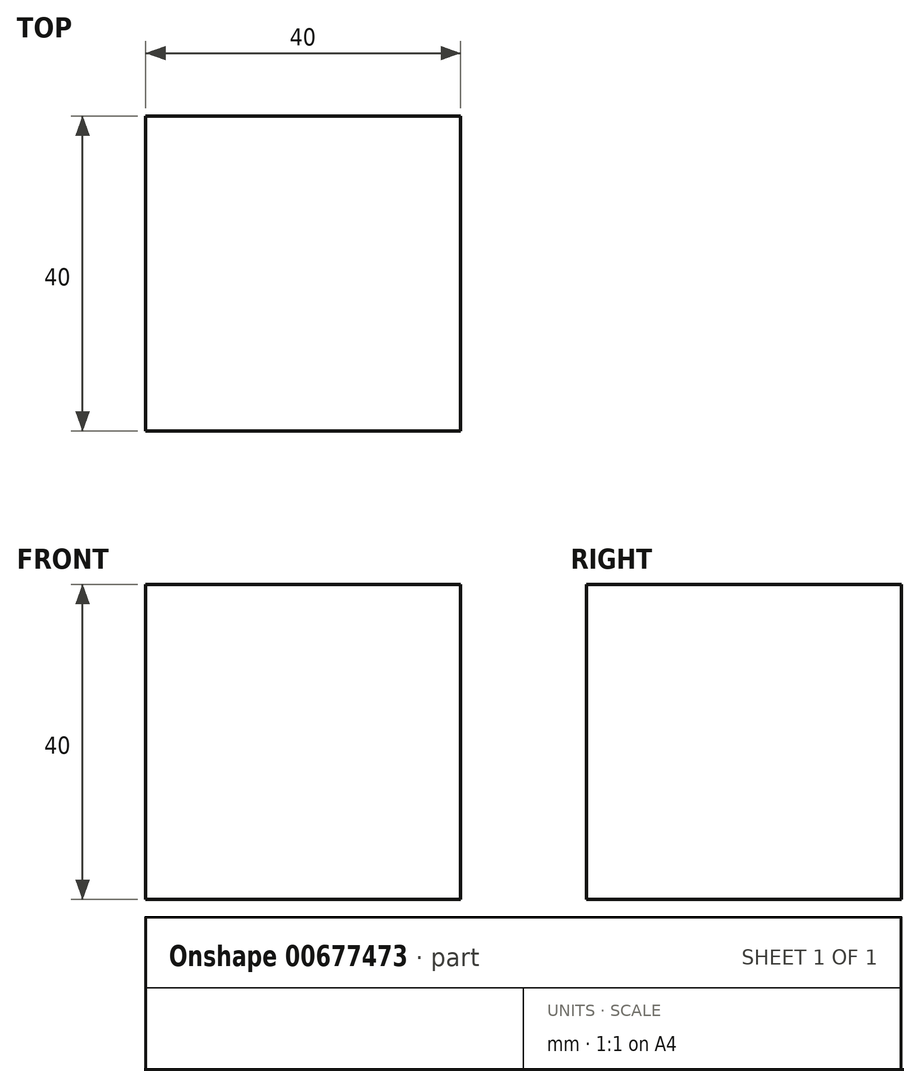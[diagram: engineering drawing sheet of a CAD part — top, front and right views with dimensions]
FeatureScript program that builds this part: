
annotation { "Feature Type Name" : "Feature", "Feature Type Description" : "" }
export const myFeature = defineFeature(function(context is Context, id is Id, definition is map)
    precondition{}
    {
        {
            var Q0;
            Q0=qCreatedBy(makeId("Front.planeOp"),FACE);
            var sketch = newSketch(context, id + "F0", { "sketchPlane" : qUnion([Q0])});
            skLineSegment(sketch, "E0.bottom", {"start": v(20, -20) * mm, "end": v(-20, -20) * mm});
            skLineSegment(sketch, "E0.top", {"start": v(20, 20) * mm, "end": v(-20, 20) * mm});
            skLineSegment(sketch, "E0.left", {"start": v(20, -20) * mm, "end": v(20, 20) * mm});
            skLineSegment(sketch, "E0.right", {"start": v(-20, -20) * mm, "end": v(-20, 20) * mm});
            skPoint(sketch, "E0.middle", {"position": v(0, 0) * mm});
            skSolve(sketch);
        }
        {
            var Q0;
            Q0=makeQuery(id+"F0.imprint","IMPRINT",FACE,{"disambiguationData":[TD([[makeQuery(id+"F0.imprint","IMPRINT",EDGE,{"derivedFrom":sQuery(id+"F0.wireOp",EDGE,"E0.bottom")}),-1.0]])]});
            extrude(context, id + "F1", {"entities" : qUnion([Q0]), "depth" : 20 * mm, "offsetDistance" : 25 * mm, "hasSecondDirection" : true, "secondDirectionOppositeDirection" : true, "secondDirectionDepth" : 20 * mm});
        }
    });
